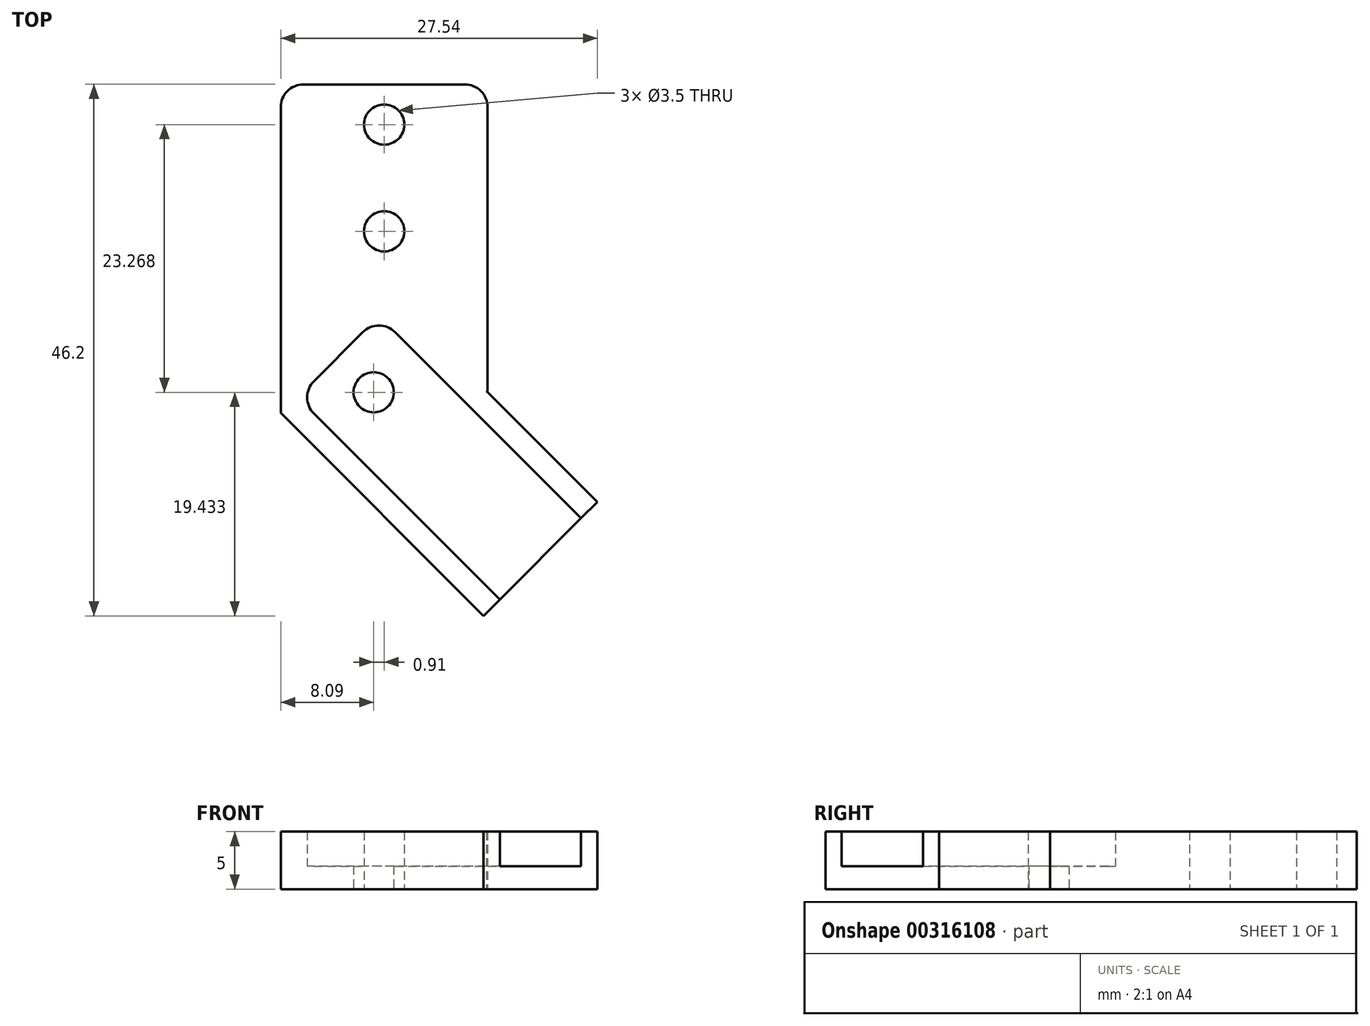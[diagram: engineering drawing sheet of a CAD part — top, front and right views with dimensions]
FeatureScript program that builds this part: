
annotation { "Feature Type Name" : "Feature", "Feature Type Description" : "" }
export const myFeature = defineFeature(function(context is Context, id is Id, definition is map)
    precondition{}
    {
        {
            var Q0;
            Q0=qCreatedBy(makeId("Top.planeOp"),FACE);
            var sketch = newSketch(context, id + "F0", { "sketchPlane" : qUnion([Q0])});
            skLineSegment(sketch, "E0.bottom", {"start": v(9, -13.33) * mm, "end": v(8.9, -13.33) * mm});
            skLineSegment(sketch, "E0.top", {"start": v(7, 13.33) * mm, "end": v(-7, 13.33) * mm});
            skLineSegment(sketch, "E0.left", {"start": v(9, -13.33) * mm, "end": v(9, 11.33) * mm});
            skLineSegment(sketch, "E0.right", {"start": v(-9, -13.33) * mm, "end": v(-9, 11.33) * mm});
            skPoint(sketch, "E0.middle", {"position": v(0, 0) * mm});
            skLineSegment(sketch, "E1.bottom", {"start": v(18.54, -22.97) * mm, "end": v(8.64, -32.87) * mm});
            skLineSegment(sketch, "E1.left", {"start": v(18.54, -22.97) * mm, "end": v(8.9, -13.33) * mm});
            skLineSegment(sketch, "E1.right", {"start": v(8.64, -32.87) * mm, "end": v(-5.5, -18.73) * mm});
            skPoint(sketch, "E1.middle", {"position": v(6.52, -20.85) * mm});
            skLineSegment(sketch, "E2", {"start": v(-5.5, -18.73) * mm, "end": v(-9, -15.23) * mm});
            skLineSegment(sketch, "E3", {"start": v(-9, -13.33) * mm, "end": v(-9, -15.23) * mm});
            skPoint(sketch, "E4.orphan", {"position": v(4.4, -8.83) * mm});
            skLineSegment(sketch, "E5.0", {"start": v(8.64, -30.04) * mm, "end": v(-4.1, -17.32) * mm});
            skLineSegment(sketch, "E5.2", {"start": v(15.7, -22.97) * mm, "end": v(7.48, -14.74) * mm});
            skLineSegment(sketch, "E6", {"start": v(8.64, -30.04) * mm, "end": v(10.05, -31.46) * mm});
            skLineSegment(sketch, "E7", {"start": v(15.7, -22.97) * mm, "end": v(17.12, -24.39) * mm});
            skLineSegment(sketch, "E8", {"start": v(7.48, -14.74) * mm, "end": v(1.65, -8.92) * mm});
            skLineSegment(sketch, "E9", {"start": v(-4.1, -17.32) * mm, "end": v(-6.11, -15.3) * mm});
            skLineSegment(sketch, "E10", {"start": v(-6.11, -12.47) * mm, "end": v(-1.87, -8.23) * mm});
            skLineSegment(sketch, "E11", {"start": v(1.65, -8.92) * mm, "end": v(0.96, -8.23) * mm});
            skLineSegment(sketch, "E12", {"start": v(-4, -10.35) * mm, "end": v(2.2, -16.55) * mm, "construction": true});
            skPoint(sketch, "E13", {"position": v(-0.91, -13.44) * mm});
            skPoint(sketch, "E14.visualSharp", {"position": v(-7.52, -13.88) * mm});
            skArc(sketch, "E14.filletArc", {"start": v(-6.11, -12.47) * mm, "mid": v(-6.7, -13.88) * mm, "end": v(-6.11, -15.3) * mm});
            skPoint(sketch, "E15.newPointA", {"position": v(-0.47, -6.82) * mm});
            skPoint(sketch, "E15.newPointB", {"position": v(-0.44, -6.82) * mm});
            skArc(sketch, "E15.filletArc", {"start": v(0.96, -8.23) * mm, "mid": v(-0.45, -7.64) * mm, "end": v(-1.87, -8.23) * mm});
            skPoint(sketch, "E16", {"position": v(0, 0.56) * mm});
            skPoint(sketch, "E17", {"position": v(0, 9.83) * mm});
            skPoint(sketch, "E18.visualSharp", {"position": v(-9, 13.33) * mm});
            skArc(sketch, "E18.filletArc", {"start": v(-7, 13.33) * mm, "mid": v(-8.41, 12.74) * mm, "end": v(-9, 11.33) * mm});
            skPoint(sketch, "E19.visualSharp", {"position": v(9, 13.33) * mm});
            skArc(sketch, "E19.filletArc", {"start": v(9, 11.33) * mm, "mid": v(8.41, 12.74) * mm, "end": v(7, 13.33) * mm});
            skSolve(sketch);
        }
        {
            var Q0;
            Q0=makeQuery(id+"F0.imprint","IMPRINT",FACE,{"disambiguationData":[TD([[makeQuery(id+"F0.imprint","IMPRINT",EDGE,{"derivedFrom":sQuery(id+"F0.wireOp",EDGE,"E5.0")}),-1.0]])]});
            extrude(context, id + "F1", {"entities" : qUnion([Q0]), "depth" : 2 * mm});
        }
        {
            var Q0;
            Q0=makeQuery(id+"F0.imprint","IMPRINT",FACE,{"disambiguationData":[TD([[makeQuery(id+"F0.imprint","IMPRINT",EDGE,{"derivedFrom":sQuery(id+"F0.wireOp",EDGE,"E0.bottom")}),-1.0]])]});
            extrude(context, id + "F2", {"entities" : qUnion([Q0]), "operationType" : NewBodyOperationType.ADD, "depth" : 5 * mm});
        }
        {
            var Q0;
            Q0=sQuery(id+"F0.wireOp",VERTEX,"E16");
            var Q1;
            Q1=sQuery(id+"F0.wireOp",VERTEX,"E13");
            var Q2;
            Q2=sQuery(id+"F0.wireOp",VERTEX,"E17");
            var Q3;
            Q3=makeQuery(id+"F1.opExtrude","SWEPT_BODY",BODY,{"disambiguationData":[OSD([sQuery(id+"F0.wireOp",EDGE,"E1.bottom"),sQuery(id+"F0.wireOp",EDGE,"E5.0"),sQuery(id+"F0.wireOp",EDGE,"E5.2"),sQuery(id+"F0.wireOp",EDGE,"E6"),sQuery(id+"F0.wireOp",EDGE,"E7"),sQuery(id+"F0.wireOp",EDGE,"E8"),sQuery(id+"F0.wireOp",EDGE,"E9"),sQuery(id+"F0.wireOp",EDGE,"E10"),sQuery(id+"F0.wireOp",EDGE,"E11"),sQuery(id+"F0.wireOp",EDGE,"E14.filletArc"),sQuery(id+"F0.wireOp",EDGE,"E15.filletArc")])]});
            hole(context, id + "F3", {"style" : HoleStyle.SIMPLE, "endStyle" : HoleEndStyle.THROUGH, "oppositeDirection" : true, "holeDiameter" : 3.5 * mm, "tappedDepth" : 12 * mm, "tapClearance" : 3, "locations" : qUnion([Q0, Q1, Q2]), "scope" : qUnion([Q3])});
        }
    });
